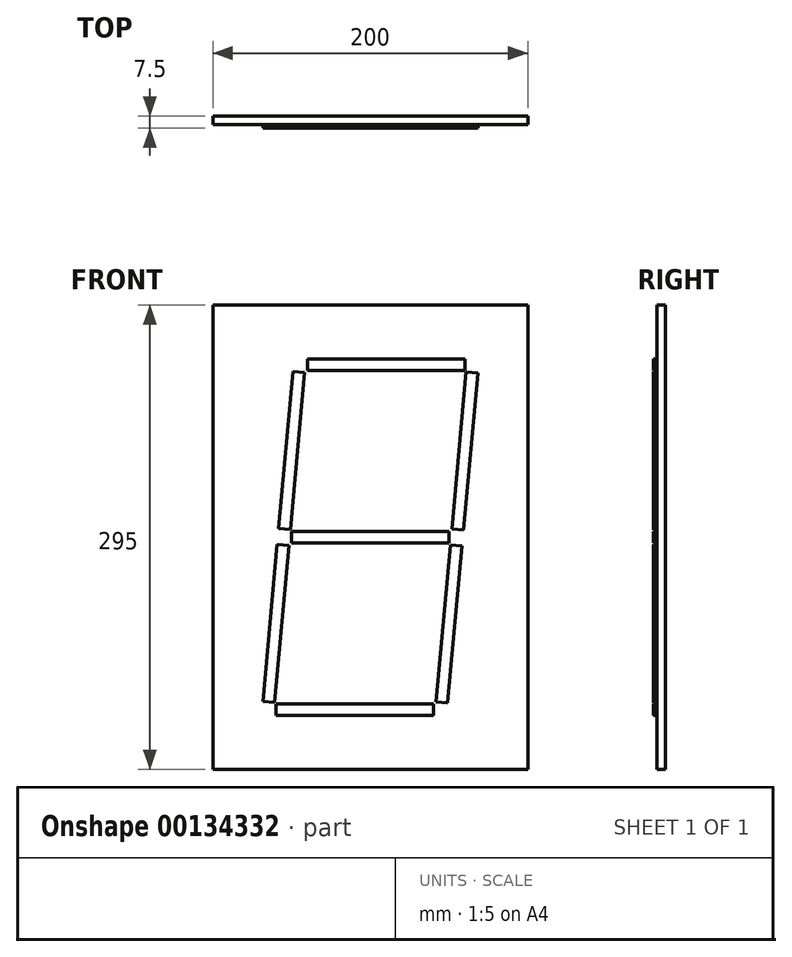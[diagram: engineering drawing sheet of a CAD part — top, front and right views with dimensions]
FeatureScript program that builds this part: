
annotation { "Feature Type Name" : "Feature", "Feature Type Description" : "" }
export const myFeature = defineFeature(function(context is Context, id is Id, definition is map)
    precondition{}
    {
        {
            var Q0;
            Q0=qCreatedBy(makeId("Front.planeOp"),FACE);
            var sketch = newSketch(context, id + "F0", { "sketchPlane" : qUnion([Q0])});
            skLineSegment(sketch, "E0", {"start": v(-100, -147.5) * mm, "end": v(100, -147.5) * mm});
            skLineSegment(sketch, "E1", {"start": v(100, -147.5) * mm, "end": v(100, 147.5) * mm});
            skLineSegment(sketch, "E2", {"start": v(100, 147.5) * mm, "end": v(-100, 147.5) * mm});
            skLineSegment(sketch, "E3", {"start": v(-100, 147.5) * mm, "end": v(-100, -147.5) * mm});
            skLineSegment(sketch, "E4", {"start": v(-58.25, 5.64) * mm, "end": v(-50.78, 4.96) * mm});
            skLineSegment(sketch, "E5", {"start": v(-50.78, 4.96) * mm, "end": v(-41.69, 104.54) * mm});
            skLineSegment(sketch, "E6", {"start": v(-41.69, 104.54) * mm, "end": v(-49.16, 105.22) * mm});
            skLineSegment(sketch, "E7", {"start": v(-49.16, 105.22) * mm, "end": v(-58.25, 5.64) * mm});
            skLineSegment(sketch, "E8", {"start": v(-40, 105.75) * mm, "end": v(60, 105.75) * mm});
            skLineSegment(sketch, "E9", {"start": v(60, 105.75) * mm, "end": v(60, 113.25) * mm});
            skLineSegment(sketch, "E10", {"start": v(60, 113.25) * mm, "end": v(-40, 113.25) * mm});
            skLineSegment(sketch, "E11", {"start": v(-40, 113.25) * mm, "end": v(-40, 105.75) * mm});
            skLineSegment(sketch, "E12", {"start": v(51.72, 5.3) * mm, "end": v(59.19, 4.62) * mm});
            skLineSegment(sketch, "E13", {"start": v(59.19, 4.62) * mm, "end": v(68.28, 104.2) * mm});
            skLineSegment(sketch, "E14", {"start": v(68.28, 104.2) * mm, "end": v(60.81, 104.88) * mm});
            skLineSegment(sketch, "E15", {"start": v(60.81, 104.88) * mm, "end": v(51.72, 5.3) * mm});
            skLineSegment(sketch, "E16", {"start": v(-50, -3.75) * mm, "end": v(50, -3.75) * mm});
            skLineSegment(sketch, "E17", {"start": v(50, -3.75) * mm, "end": v(50, 3.75) * mm});
            skLineSegment(sketch, "E18", {"start": v(50, 3.75) * mm, "end": v(-50, 3.75) * mm});
            skLineSegment(sketch, "E19", {"start": v(-50, 3.75) * mm, "end": v(-50, -3.75) * mm});
            skLineSegment(sketch, "E20", {"start": v(-60, -113.25) * mm, "end": v(40, -113.25) * mm});
            skLineSegment(sketch, "E21", {"start": v(40, -113.25) * mm, "end": v(40, -105.75) * mm});
            skLineSegment(sketch, "E22", {"start": v(40, -105.75) * mm, "end": v(-60, -105.75) * mm});
            skLineSegment(sketch, "E23", {"start": v(-60, -105.75) * mm, "end": v(-60, -113.25) * mm});
            skLineSegment(sketch, "E24", {"start": v(-68.28, -104.2) * mm, "end": v(-60.81, -104.88) * mm});
            skLineSegment(sketch, "E25", {"start": v(-60.81, -104.88) * mm, "end": v(-51.72, -5.3) * mm});
            skLineSegment(sketch, "E26", {"start": v(-51.72, -5.3) * mm, "end": v(-59.19, -4.62) * mm});
            skLineSegment(sketch, "E27", {"start": v(-59.19, -4.62) * mm, "end": v(-68.28, -104.2) * mm});
            skLineSegment(sketch, "E28", {"start": v(41.69, -104.54) * mm, "end": v(49.16, -105.22) * mm});
            skLineSegment(sketch, "E29", {"start": v(49.16, -105.22) * mm, "end": v(58.25, -5.64) * mm});
            skLineSegment(sketch, "E30", {"start": v(58.25, -5.64) * mm, "end": v(50.78, -4.96) * mm});
            skLineSegment(sketch, "E31", {"start": v(50.78, -4.96) * mm, "end": v(41.69, -104.54) * mm});
            skSolve(sketch);
        }
        {
            var Q0;
            Q0=makeQuery(id+"F0.imprint","IMPRINT",FACE,{"disambiguationData":[TD([[makeQuery(id+"F0.imprint","IMPRINT",EDGE,{"derivedFrom":sQuery(id+"F0.wireOp",EDGE,"E8")}),1.0]])]});
            var Q1;
            Q1=makeQuery(id+"F0.imprint","IMPRINT",FACE,{"disambiguationData":[TD([[makeQuery(id+"F0.imprint","IMPRINT",EDGE,{"derivedFrom":sQuery(id+"F0.wireOp",EDGE,"E4")}),1.0]])]});
            var Q2;
            Q2=makeQuery(id+"F0.imprint","IMPRINT",FACE,{"disambiguationData":[TD([[makeQuery(id+"F0.imprint","IMPRINT",EDGE,{"derivedFrom":sQuery(id+"F0.wireOp",EDGE,"E12")}),1.0]])]});
            var Q3;
            Q3=makeQuery(id+"F0.imprint","IMPRINT",FACE,{"disambiguationData":[TD([[makeQuery(id+"F0.imprint","IMPRINT",EDGE,{"derivedFrom":sQuery(id+"F0.wireOp",EDGE,"E16")}),1.0]])]});
            var Q4;
            Q4=makeQuery(id+"F0.imprint","IMPRINT",FACE,{"disambiguationData":[TD([[makeQuery(id+"F0.imprint","IMPRINT",EDGE,{"derivedFrom":sQuery(id+"F0.wireOp",EDGE,"E24")}),1.0]])]});
            var Q5;
            Q5=makeQuery(id+"F0.imprint","IMPRINT",FACE,{"disambiguationData":[TD([[makeQuery(id+"F0.imprint","IMPRINT",EDGE,{"derivedFrom":sQuery(id+"F0.wireOp",EDGE,"E20")}),1.0]])]});
            var Q6;
            Q6=makeQuery(id+"F0.imprint","IMPRINT",FACE,{"disambiguationData":[TD([[makeQuery(id+"F0.imprint","IMPRINT",EDGE,{"derivedFrom":sQuery(id+"F0.wireOp",EDGE,"E28")}),1.0]])]});
            extrude(context, id + "F1", {"entities" : qUnion([Q0, Q1, Q2, Q3, Q4, Q5, Q6]), "depth" : 2 * mm});
        }
        {
            var Q0;
            Q0=qCreatedBy(makeId("Front.planeOp"),FACE);
            var sketch = newSketch(context, id + "F2", { "sketchPlane" : qUnion([Q0])});
            skLineSegment(sketch, "E32.bottom", {"start": v(-100, 147.5) * mm, "end": v(100, 147.5) * mm});
            skLineSegment(sketch, "E32.top", {"start": v(-100, -147.5) * mm, "end": v(100, -147.5) * mm});
            skLineSegment(sketch, "E32.left", {"start": v(-100, 147.5) * mm, "end": v(-100, -147.5) * mm});
            skLineSegment(sketch, "E32.right", {"start": v(100, 147.5) * mm, "end": v(100, -147.5) * mm});
            skSolve(sketch);
        }
        {
            var Q0;
            Q0 = qSketchRegion(id + "F2", true);
            var Q1;
            Q1=sQuery(id+"F0.wireOp",EDGE,"E2");
            var Q2;
            Q2=sQuery(id+"F0.wireOp",EDGE,"E3");
            var Q3;
            Q3=sQuery(id+"F0.wireOp",EDGE,"E0");
            var Q4;
            Q4=sQuery(id+"F0.wireOp",EDGE,"E1");
            extrude(context, id + "F3", {"entities" : qUnion([Q0]), "surfaceEntities" : qUnion([Q1, Q2, Q3, Q4]), "oppositeDirection" : true, "depth" : 5.5 * mm});
        }
    });
